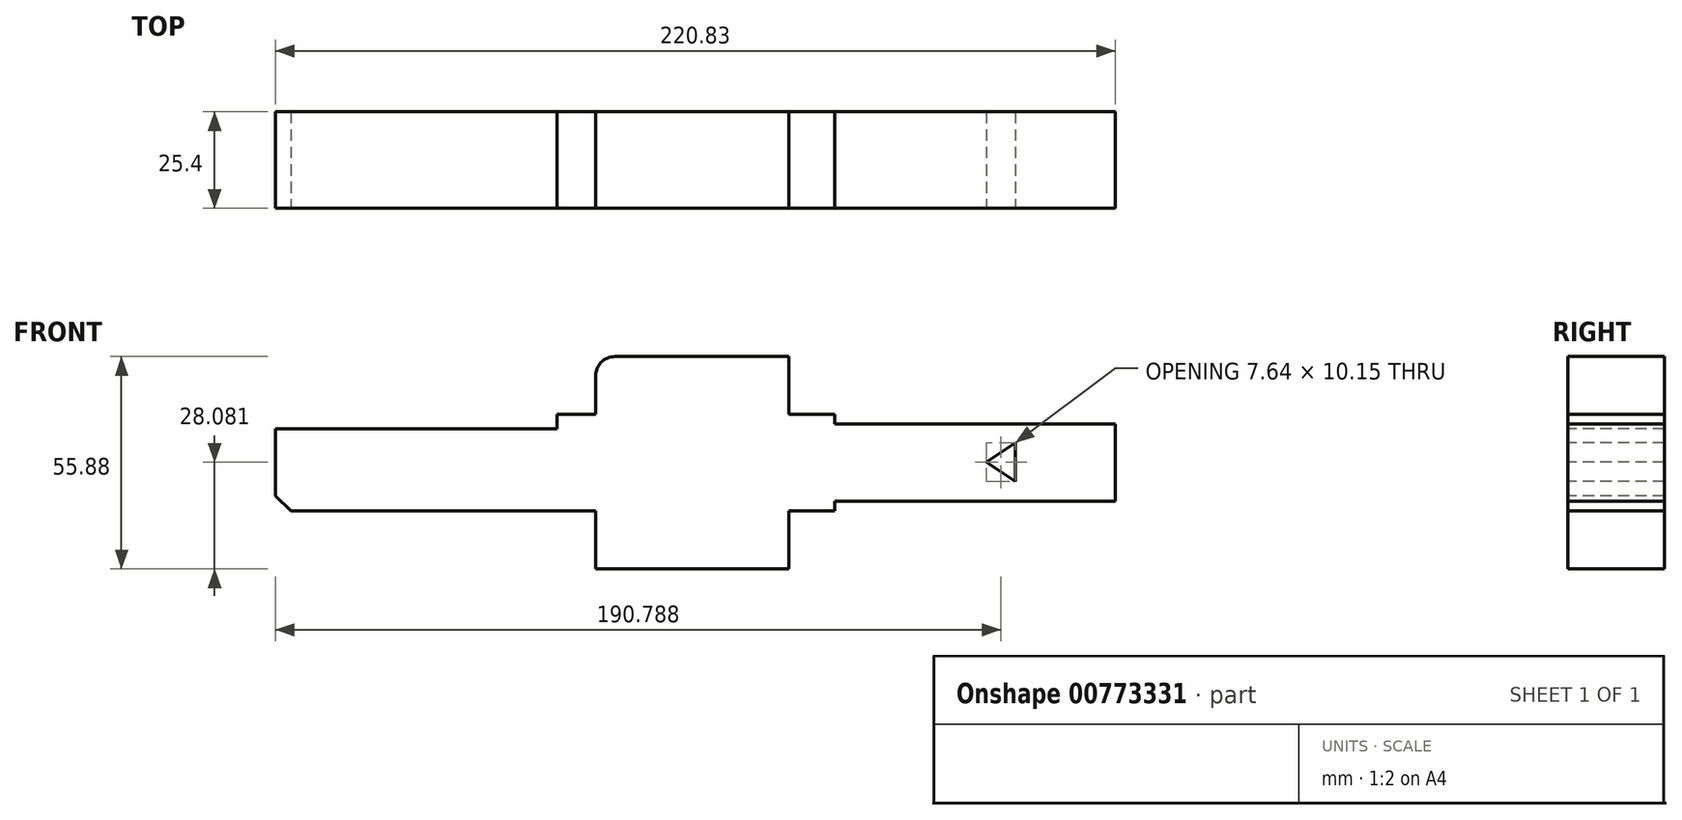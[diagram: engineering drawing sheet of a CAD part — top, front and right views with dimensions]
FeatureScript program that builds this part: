
annotation { "Feature Type Name" : "Feature", "Feature Type Description" : "" }
export const myFeature = defineFeature(function(context is Context, id is Id, definition is map)
    precondition{}
    {
        {
            var Q0;
            Q0=qCreatedBy(makeId("Front.planeOp"),FACE);
            var sketch = newSketch(context, id + "F0", { "sketchPlane" : qUnion([Q0])});
            skLineSegment(sketch, "E0", {"start": v(-69.97, -15.86) * mm, "end": v(10.16, -15.86) * mm});
            skLineSegment(sketch, "E1", {"start": v(10.16, -15.86) * mm, "end": v(10.16, 9.54) * mm});
            skLineSegment(sketch, "E2", {"start": v(10.16, 9.54) * mm, "end": v(0, 9.54) * mm});
            skLineSegment(sketch, "E3", {"start": v(0, 9.54) * mm, "end": v(0, 5.8) * mm});
            skLineSegment(sketch, "E4", {"start": v(0, 5.8) * mm, "end": v(-69.97, 5.8) * mm});
            skLineSegment(sketch, "E5", {"start": v(-69.97, 5.8) * mm, "end": v(-69.97, -15.86) * mm});
            skLineSegment(sketch, "E6", {"start": v(-69.97, -15.86) * mm, "end": v(-74, -11.83) * mm});
            skLineSegment(sketch, "E7", {"start": v(-74, -11.83) * mm, "end": v(-74, 5.8) * mm});
            skLineSegment(sketch, "E8", {"start": v(-74, 5.8) * mm, "end": v(-69.97, 5.8) * mm});
            skLineSegment(sketch, "E9", {"start": v(-51.45, 5.8) * mm, "end": v(-51.45, -15.86) * mm});
            skLineSegment(sketch, "E10", {"start": v(-39.4, 5.8) * mm, "end": v(-39.4, -15.86) * mm});
            skLineSegment(sketch, "E11", {"start": v(10.16, 9.54) * mm, "end": v(10.16, 24.78) * mm});
            skLineSegment(sketch, "E12", {"start": v(10.16, 24.78) * mm, "end": v(60.96, 24.78) * mm});
            skLineSegment(sketch, "E13", {"start": v(60.96, 24.78) * mm, "end": v(60.96, -31.1) * mm});
            skLineSegment(sketch, "E14", {"start": v(60.96, -31.1) * mm, "end": v(10.16, -31.1) * mm});
            skLineSegment(sketch, "E15", {"start": v(10.16, -31.1) * mm, "end": v(10.16, -15.86) * mm});
            skLineSegment(sketch, "E16", {"start": v(60.96, 9.54) * mm, "end": v(73.11, 9.54) * mm});
            skLineSegment(sketch, "E17", {"start": v(73.11, 9.54) * mm, "end": v(73.11, -15.86) * mm});
            skLineSegment(sketch, "E18", {"start": v(72.39, 7.1) * mm, "end": v(146.83, 7.1) * mm});
            skLineSegment(sketch, "E19", {"start": v(146.83, 7.1) * mm, "end": v(146.83, -13.22) * mm});
            skLineSegment(sketch, "E20", {"start": v(146.83, -13.22) * mm, "end": v(73.11, -13.22) * mm});
            skLineSegment(sketch, "E21", {"start": v(73.11, -15.86) * mm, "end": v(60.96, -15.86) * mm});
            skLineSegment(sketch, "E22", {"start": v(146.24, 2.06) * mm, "end": v(120.6, 2.06) * mm});
            skLineSegment(sketch, "E23", {"start": v(120.6, 2.06) * mm, "end": v(120.6, -8.1) * mm});
            skLineSegment(sketch, "E24", {"start": v(120.6, -8.1) * mm, "end": v(146.66, -8.1) * mm});
            skLineSegment(sketch, "E25", {"start": v(120.6, 2.06) * mm, "end": v(112.97, -3.02) * mm});
            skPoint(sketch, "E25.endSnap0", {"position": v(120.6, -3.02) * mm});
            skLineSegment(sketch, "E26", {"start": v(112.97, -3.02) * mm, "end": v(120.6, -8.1) * mm});
            skLineSegment(sketch, "E27", {"start": v(19.08, 24.78) * mm, "end": v(19.08, 9.34) * mm});
            skLineSegment(sketch, "E28", {"start": v(19.08, 9.34) * mm, "end": v(31.08, 9.34) * mm});
            skLineSegment(sketch, "E29", {"start": v(31.08, -15.51) * mm, "end": v(20.16, -15.73) * mm});
            skLineSegment(sketch, "E30", {"start": v(20.16, -15.73) * mm, "end": v(20.16, -31.1) * mm});
            skLineSegment(sketch, "E31", {"start": v(51.65, 24.78) * mm, "end": v(51.65, 9.34) * mm});
            skLineSegment(sketch, "E32", {"start": v(51.65, 9.34) * mm, "end": v(42.65, 9.13) * mm});
            skLineSegment(sketch, "E33", {"start": v(42.65, 9.13) * mm, "end": v(42.65, -15.74) * mm});
            skLineSegment(sketch, "E34", {"start": v(42.65, -15.74) * mm, "end": v(51.87, -15.74) * mm});
            skLineSegment(sketch, "E35", {"start": v(51.87, -15.74) * mm, "end": v(51.87, -31.38) * mm});
            skLineSegment(sketch, "E36", {"start": v(31.08, 9.34) * mm, "end": v(31.08, -15.51) * mm});
            skLineSegment(sketch, "E37", {"start": v(0, 74.63) * mm, "end": v(0, 35.42) * mm});
            skSolve(sketch);
        }
        {
            var Q0;
            Q0 = qSketchRegion(id + "F0", true);
            var Q1;
            Q1=sQuery(id+"F0.wireOp",EDGE,"E4");
            var Q2;
            Q2=sQuery(id+"F0.wireOp",EDGE,"E10");
            var Q3;
            Q3=sQuery(id+"F0.wireOp",EDGE,"E9");
            var Q4;
            Q4=sQuery(id+"F0.wireOp",EDGE,"E5");
            var Q5;
            Q5=sQuery(id+"F0.wireOp",EDGE,"E7");
            var Q6;
            Q6=sQuery(id+"F0.wireOp",EDGE,"E13");
            var Q7;
            Q7=sQuery(id+"F0.wireOp",EDGE,"E28");
            var Q8;
            Q8=sQuery(id+"F0.wireOp",EDGE,"E36");
            var Q9;
            Q9=sQuery(id+"F0.wireOp",EDGE,"E14");
            var Q10;
            Q10=sQuery(id+"F0.wireOp",EDGE,"E30");
            var Q11;
            Q11=sQuery(id+"F0.wireOp",EDGE,"E0");
            var Q12;
            Q12=sQuery(id+"F0.wireOp",EDGE,"E1");
            var Q13;
            Q13=sQuery(id+"F0.wireOp",EDGE,"E27");
            var Q14;
            Q14=sQuery(id+"F0.wireOp",EDGE,"E12");
            extrude(context, id + "F1", {"entities" : qUnion([Q0]), "surfaceEntities" : qUnion([Q1, Q2, Q3, Q4, Q5, Q6, Q7, Q8, Q9, Q10, Q11, Q12, Q13, Q14]), "oppositeDirection" : true, "depth" : 25.4 * mm, "offsetDistance" : 25.4 * mm});
        }
        {
            var Q0;
            Q0=makeQuery(id+"F1.opExtrude","SWEPT_EDGE",EDGE,{"disambiguationData":[OSD([sQuery(id+"F0.wireOp",EDGE,"E11"),sQuery(id+"F0.wireOp",EDGE,"E12")])]});
            fillet(context, id + "F2", {"entities" : qUnion([Q0]), "radius" : 5.08 * mm, "tangentPropagation" : true, "allowEdgeOverflow" : false});
        }
    });
